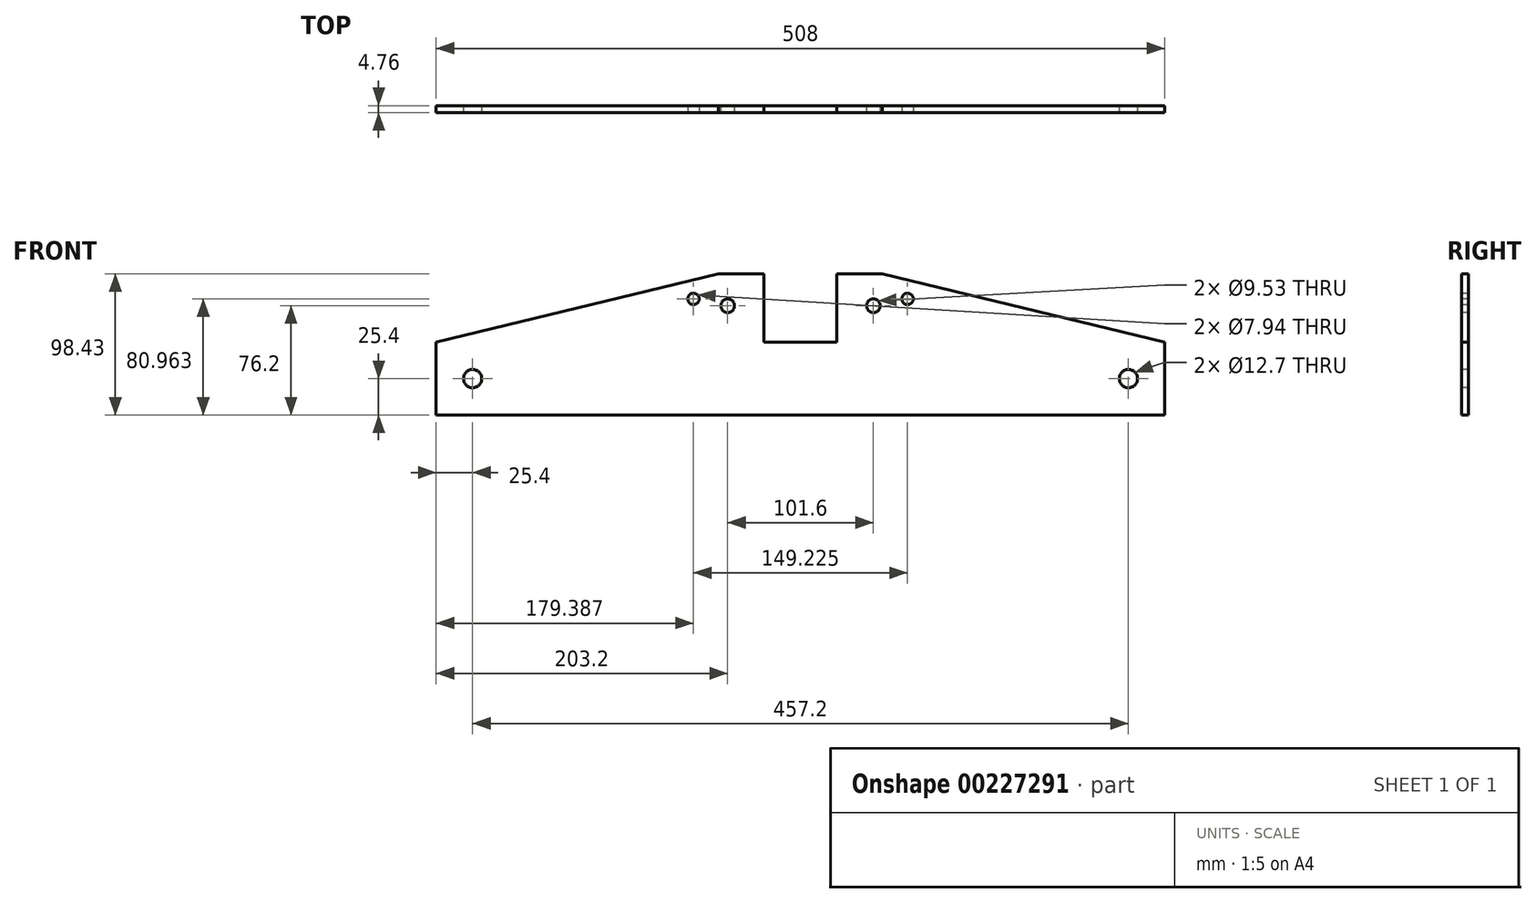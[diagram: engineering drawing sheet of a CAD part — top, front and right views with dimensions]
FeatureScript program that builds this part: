
annotation { "Feature Type Name" : "Feature", "Feature Type Description" : "" }
export const myFeature = defineFeature(function(context is Context, id is Id, definition is map)
    precondition{}
    {
        {
            var Q0;
            Q0=qCreatedBy(makeId("Front.planeOp"),FACE);
            var sketch = newSketch(context, id + "F0", { "sketchPlane" : qUnion([Q0])});
            skLineSegment(sketch, "E0", {"start": v(0, 0) * mm, "end": v(25.4, 0) * mm});
            skLineSegment(sketch, "E1", {"start": v(25.4, 0) * mm, "end": v(25.4, 47.63) * mm});
            skLineSegment(sketch, "E2", {"start": v(25.4, 47.62) * mm, "end": v(57.15, 47.62) * mm});
            skLineSegment(sketch, "E3", {"start": v(57.15, 47.62) * mm, "end": v(254, 0) * mm});
            skLineSegment(sketch, "E4", {"start": v(254, 0) * mm, "end": v(254, -50.8) * mm});
            skLineSegment(sketch, "E5", {"start": v(254, -50.8) * mm, "end": v(0, -50.8) * mm});
            skLineSegment(sketch, "E6", {"start": v(0, -50.8) * mm, "end": v(0, 0) * mm});
            skSolve(sketch);
        }
        {
            var Q0;
            Q0=makeQuery(id+"F0.imprint","IMPRINT",FACE,{"disambiguationData":[TD([[makeQuery(id+"F0.imprint","IMPRINT",EDGE,{"derivedFrom":sQuery(id+"F0.wireOp",EDGE,"E0")}),-1.0]])]});
            extrude(context, id + "F1", {"entities" : qUnion([Q0]), "oppositeDirection" : true, "depth" : 4.76 * mm});
        }
        {
            var Q0;
            Q0=qCreatedBy(makeId("Front.planeOp"),FACE);
            var sketch = newSketch(context, id + "F2", { "sketchPlane" : qUnion([Q0])});
            skCircle(sketch, "E7", {"center": v(228.6, -25.4) * mm, "radius": 6.35 * mm});
            skCircle(sketch, "E8", {"center": v(74.61, 30.16) * mm, "radius": 3.97 * mm});
            skCircle(sketch, "E9", {"center": v(50.8, 25.4) * mm, "radius": 4.76 * mm});
            skSolve(sketch);
        }
        {
            var Q0;
            Q0 = qSketchRegion(id + "F2", true);
            extrude(context, id + "F3", {"entities" : qUnion([Q0]), "operationType" : NewBodyOperationType.REMOVE, "endBound" : BoundingType.THROUGH_ALL, "oppositeDirection" : true, "depth" : 25.4 * mm});
        }
        {
            var Q0;
            Q0=makeQuery(id+"F1.opExtrude","SWEPT_BODY",BODY,{"disambiguationData":[OSD([sQuery(id+"F0.wireOp",EDGE,"E0"),sQuery(id+"F0.wireOp",EDGE,"E1"),sQuery(id+"F0.wireOp",EDGE,"E2"),sQuery(id+"F0.wireOp",EDGE,"E3"),sQuery(id+"F0.wireOp",EDGE,"E4"),sQuery(id+"F0.wireOp",EDGE,"E5"),sQuery(id+"F0.wireOp",EDGE,"E6")])]});
            var Q1;
            Q1=qCreatedBy(makeId("Right.planeOp"),FACE);
            mirror(context, id + "F4", {"operationType" : NewBodyOperationType.ADD, "entities" : qUnion([Q0]), "mirrorPlane" : qUnion([Q1])});
        }
    });
